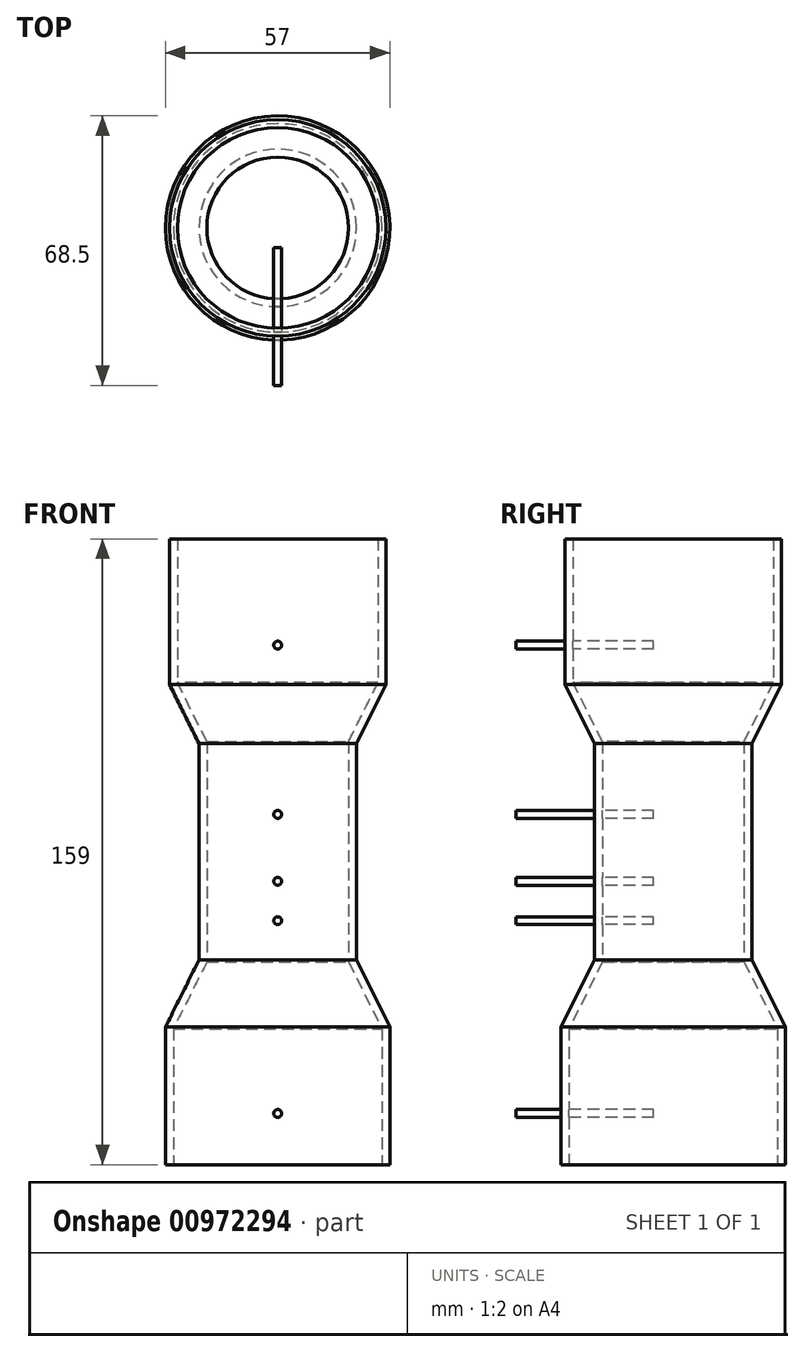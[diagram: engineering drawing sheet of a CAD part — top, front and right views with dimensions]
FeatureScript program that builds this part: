
annotation { "Feature Type Name" : "Feature", "Feature Type Description" : "" }
export const myFeature = defineFeature(function(context is Context, id is Id, definition is map)
    precondition{}
    {
        {
            var Q0;
            Q0=qCreatedBy(makeId("Top.planeOp"),FACE);
            cPlane(context, id + "F0", {"entities" : qUnion([Q0]), "cplaneType" : CPlaneType.OFFSET, "offset" : 35 * mm, "width" : 150 * mm, "height" : 150 * mm});
        }
        {
            var Q0;
            Q0=qCreatedBy(makeId("Top.planeOp"),FACE);
            cPlane(context, id + "F1", {"entities" : qUnion([Q0]), "cplaneType" : CPlaneType.OFFSET, "offset" : 52 * mm, "width" : 150 * mm, "height" : 150 * mm});
        }
        {
            var Q0;
            Q0=qCreatedBy(makeId("Top.planeOp"),FACE);
            cPlane(context, id + "F2", {"entities" : qUnion([Q0]), "cplaneType" : CPlaneType.OFFSET, "offset" : 107 * mm, "width" : 150 * mm, "height" : 150 * mm});
        }
        {
            var Q0;
            Q0=qCreatedBy(id+"F2.planeOp",FACE);
            cPlane(context, id + "F3", {"entities" : qUnion([Q0]), "cplaneType" : CPlaneType.OFFSET, "offset" : 15 * mm, "width" : 150 * mm, "height" : 150 * mm});
        }
        {
            var Q0;
            Q0=qCreatedBy(id+"F3.planeOp",FACE);
            cPlane(context, id + "F4", {"entities" : qUnion([Q0]), "cplaneType" : CPlaneType.OFFSET, "offset" : 37 * mm, "width" : 150 * mm, "height" : 150 * mm});
        }
        {
            var Q0;
            Q0=qCreatedBy(makeId("Right.planeOp"),FACE);
            var sketch = newSketch(context, id + "F5", { "sketchPlane" : qUnion([Q0])});
            skLineSegment(sketch, "E0", {"start": v(28.5, 0) * mm, "end": v(0, 0) * mm});
            skLineSegment(sketch, "E1", {"start": v(0, 0) * mm, "end": v(0, 159) * mm});
            skLineSegment(sketch, "E2", {"start": v(28.5, 0) * mm, "end": v(28.5, 35) * mm});
            skLineSegment(sketch, "E3", {"start": v(28.5, 35) * mm, "end": v(20, 52) * mm});
            skLineSegment(sketch, "E4", {"start": v(20, 52) * mm, "end": v(20, 107) * mm});
            skLineSegment(sketch, "E5", {"start": v(20, 107) * mm, "end": v(27.5, 122) * mm});
            skLineSegment(sketch, "E6", {"start": v(27.5, 122) * mm, "end": v(27.5, 159) * mm});
            skLineSegment(sketch, "E7", {"start": v(27.5, 159) * mm, "end": v(0, 159) * mm});
            skSolve(sketch);
        }
        {
            var Q0;
            Q0=makeQuery(id+"F5.imprint","IMPRINT",FACE,{"disambiguationData":[TD([[makeQuery(id+"F5.imprint","IMPRINT",EDGE,{"derivedFrom":sQuery(id+"F5.wireOp",EDGE,"E0")}),-1.0]])]});
            var Q1;
            Q1=sQuery(id+"F5.wireOp",EDGE,"E1");
            revolve(context, id + "F6", {"surfaceOperationType" : NewSurfaceOperationType.NEW, "entities" : qUnion([Q0]), "axis" : qUnion([Q1]), "revolveType" : RevolveType.ONE_DIRECTION, "angle" : 360 * degree});
        }
        {
            var Q0;
            Q0=makeQuery(id+"F6.opRevolve","CAP_FACE",FACE,{"disambiguationData":[OSD([sQuery(id+"F5.wireOp",EDGE,"E0"),sQuery(id+"F5.wireOp",EDGE,"E1"),sQuery(id+"F5.wireOp",EDGE,"E2"),sQuery(id+"F5.wireOp",EDGE,"E3"),sQuery(id+"F5.wireOp",EDGE,"E4"),sQuery(id+"F5.wireOp",EDGE,"E5"),sQuery(id+"F5.wireOp",EDGE,"E6"),sQuery(id+"F5.wireOp",EDGE,"E7")])],"isStart":true});
            var Q1;
            Q1=makeQuery(id+"F6.opRevolve","SWEPT_FACE",FACE,{"disambiguationData":[OSD([sQuery(id+"F5.wireOp",EDGE,"E7")])]});
            var Q2;
            Q2=makeQuery(id+"F6.opRevolve","CAP_FACE",FACE,{"disambiguationData":[OSD([sQuery(id+"F5.wireOp",EDGE,"E0"),sQuery(id+"F5.wireOp",EDGE,"E1"),sQuery(id+"F5.wireOp",EDGE,"E2"),sQuery(id+"F5.wireOp",EDGE,"E3"),sQuery(id+"F5.wireOp",EDGE,"E4"),sQuery(id+"F5.wireOp",EDGE,"E5"),sQuery(id+"F5.wireOp",EDGE,"E6"),sQuery(id+"F5.wireOp",EDGE,"E7")])],"isStart":false});
            var Q3;
            Q3=makeQuery(id+"F6.opRevolve","SWEPT_FACE",FACE,{"disambiguationData":[OSD([sQuery(id+"F5.wireOp",EDGE,"E0")])]});
            shell(context, id + "F7", {"entities" : qUnion([Q0, Q1, Q2, Q3]), "thickness" : 2 * mm});
        }
        {
            var Q0;
            Q0=qCreatedBy(makeId("Front.planeOp"),FACE);
            cPlane(context, id + "F8", {"entities" : qUnion([Q0]), "cplaneType" : CPlaneType.OFFSET, "offset" : 40 * mm, "width" : 150 * mm, "height" : 150 * mm});
        }
        {
            var Q0;
            Q0=qCreatedBy(id+"F8.planeOp",FACE);
            var sketch = newSketch(context, id + "F9", { "sketchPlane" : qUnion([Q0])});
            skCircle(sketch, "E8", {"center": v(0, 13) * mm, "radius": 1 * mm});
            skCircle(sketch, "E9", {"center": v(0, 89) * mm, "radius": 1 * mm});
            skCircle(sketch, "E10", {"center": v(0, 62) * mm, "radius": 1 * mm});
            skCircle(sketch, "E11", {"center": v(0, 72) * mm, "radius": 1 * mm});
            skCircle(sketch, "E12", {"center": v(0, 132) * mm, "radius": 1 * mm});
            skSolve(sketch);
        }
        {
            var Q0;
            Q0=makeQuery(id+"F6.opRevolve","SWEPT_BODY",BODY,{"disambiguationData":[OSD([sQuery(id+"F5.wireOp",EDGE,"E0"),sQuery(id+"F5.wireOp",EDGE,"E1"),sQuery(id+"F5.wireOp",EDGE,"E2"),sQuery(id+"F5.wireOp",EDGE,"E3"),sQuery(id+"F5.wireOp",EDGE,"E4"),sQuery(id+"F5.wireOp",EDGE,"E5"),sQuery(id+"F5.wireOp",EDGE,"E6"),sQuery(id+"F5.wireOp",EDGE,"E7")])]});
            transform(context, id + "F10", {"entities" : qUnion([Q0]), "transformType" : TransformType.TRANSLATION_3D, "dx" : 0 * mm, "dy" : 0 * mm, "dz" : 0 * mm, "makeCopy" : true});
        }
        {
            var Q0;
            Q0=qSketchRegion(id+"F9",true);
            extrude(context, id + "F11", {"entities" : qUnion([Q0]), "operationType" : NewBodyOperationType.ADD, "oppositeDirection" : true, "offsetDistance" : 25 * mm, "depth" : 35 * mm});
        }
    });
